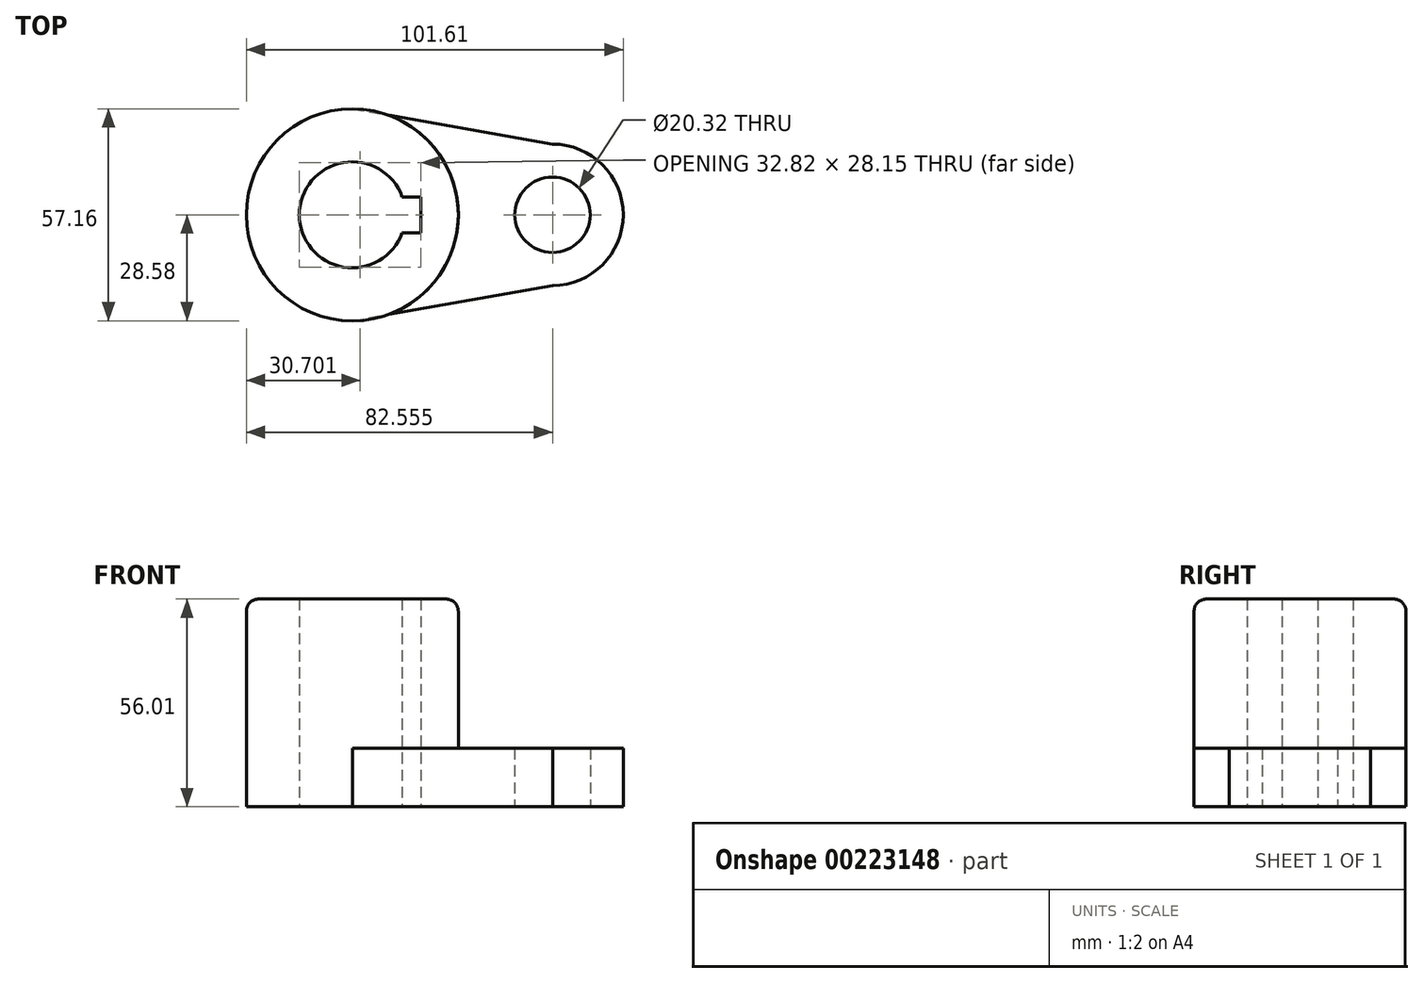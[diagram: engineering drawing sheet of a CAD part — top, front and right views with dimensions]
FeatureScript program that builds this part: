
annotation { "Feature Type Name" : "Feature", "Feature Type Description" : "" }
export const myFeature = defineFeature(function(context is Context, id is Id, definition is map)
    precondition{}
    {
        {
            var Q0;
            Q0=qCreatedBy(makeId("Top.planeOp"),FACE);
            var sketch = newSketch(context, id + "F0", { "sketchPlane" : qUnion([Q0])});
            skArc(sketch, "E0", {"start": v(13.45, 4.83) * mm, "mid": v(-14.29, 0) * mm, "end": v(13.45, -4.83) * mm});
            skCircle(sketch, "E1", {"center": v(53.98, 0) * mm, "radius": 10.16 * mm});
            skArc(sketch, "E2", {"start": v(0, 28.58) * mm, "mid": v(-28.58, 0) * mm, "end": v(0, -28.58) * mm});
            skLineSegment(sketch, "E3", {"start": v(18.53, 4.83) * mm, "end": v(18.53, -4.83) * mm});
            skLineSegment(sketch, "E4", {"start": v(18.53, 4.83) * mm, "end": v(13.45, 4.83) * mm});
            skLineSegment(sketch, "E5", {"start": v(18.53, -4.83) * mm, "end": v(13.45, -4.83) * mm});
            skArc(sketch, "E6", {"start": v(53.98, 19.05) * mm, "mid": v(73.03, 0) * mm, "end": v(53.98, -19.05) * mm});
            skLineSegment(sketch, "E7", {"start": v(0, 28.58) * mm, "end": v(53.97, 19.05) * mm});
            skLineSegment(sketch, "E8", {"start": v(0, -28.58) * mm, "end": v(53.97, -19.05) * mm});
            skSolve(sketch);
        }
        {
            var Q0;
            Q0 = qSketchRegion(id + "F0", true);
            extrude(context, id + "F1", {"entities" : qUnion([Q0]), "depth" : 15.77 * mm});
        }
        {
            var Q0;
            Q0=makeQuery(id+"F1.opExtrude","CAP_FACE",FACE,{"disambiguationData":[OSD([sQuery(id+"F0.wireOp",EDGE,"E0"),sQuery(id+"F0.wireOp",EDGE,"E1"),sQuery(id+"F0.wireOp",EDGE,"E2"),sQuery(id+"F0.wireOp",EDGE,"E3"),sQuery(id+"F0.wireOp",EDGE,"E4"),sQuery(id+"F0.wireOp",EDGE,"E5"),sQuery(id+"F0.wireOp",EDGE,"E6"),sQuery(id+"F0.wireOp",EDGE,"E7"),sQuery(id+"F0.wireOp",EDGE,"E8")])],"isStart":false});
            var sketch = newSketch(context, id + "F2", { "sketchPlane" : qUnion([Q0])});
            skCircle(sketch, "E9", {"center": v(0, 0) * mm, "radius": 28.58 * mm});
            skArc(sketch, "E10", {"start": v(13.45, 4.83) * mm, "mid": v(-14.29, 0) * mm, "end": v(13.45, -4.83) * mm});
            skLineSegment(sketch, "E11", {"start": v(13.45, 4.83) * mm, "end": v(18.53, 4.83) * mm});
            skLineSegment(sketch, "E12", {"start": v(18.53, 4.83) * mm, "end": v(18.53, -4.83) * mm});
            skLineSegment(sketch, "E13", {"start": v(18.53, -4.83) * mm, "end": v(13.45, -4.83) * mm});
            skSolve(sketch);
        }
        {
            var Q0;
            Q0 = qSketchRegion(id + "F2", true);
            extrude(context, id + "F3", {"entities" : qUnion([Q0]), "operationType" : NewBodyOperationType.ADD, "depth" : 40.23 * mm});
        }
        {
            var Q0;
            Q0=makeQuery(id+"F3.opExtrude","CAP_EDGE",EDGE,{"disambiguationData":[OSD([sQuery(id+"F2.wireOp",EDGE,"E9")])],"isStart":false});
            fillet(context, id + "F4", {"entities" : qUnion([Q0]), "radius" : 3.3 * mm, "tangentPropagation" : true, "allowEdgeOverflow" : false});
        }
    });
